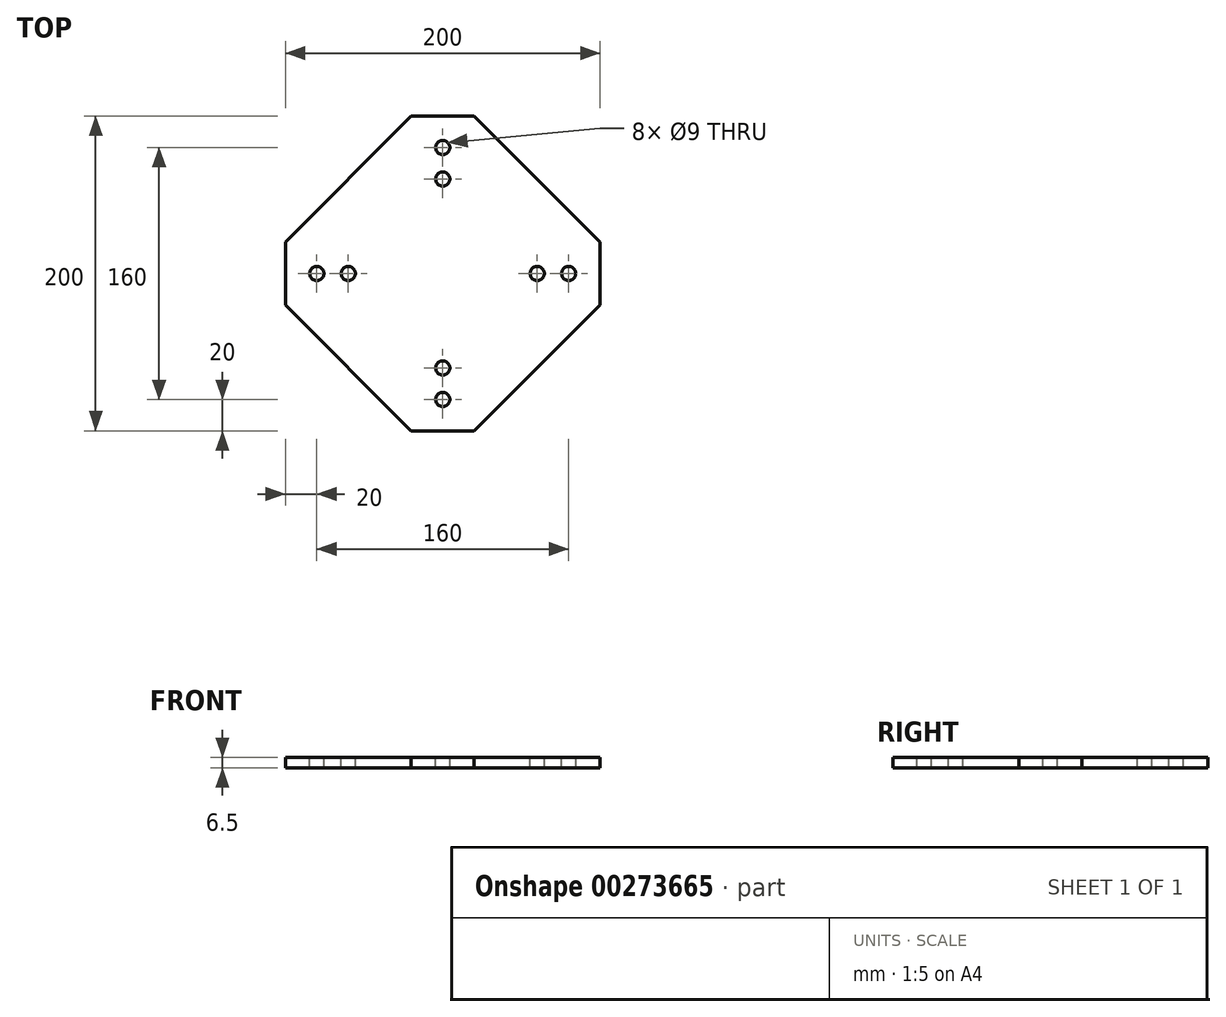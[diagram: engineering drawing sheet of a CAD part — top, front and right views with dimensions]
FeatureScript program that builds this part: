
annotation { "Feature Type Name" : "Feature", "Feature Type Description" : "" }
export const myFeature = defineFeature(function(context is Context, id is Id, definition is map)
    precondition{}
    {
        {
            var Q0;
            Q0=qCreatedBy(makeId("Top.planeOp"),FACE);
            var sketch = newSketch(context, id + "F0", { "sketchPlane" : qUnion([Q0])});
            skLineSegment(sketch, "E0", {"start": v(-100, 20) * mm, "end": v(-20, 100) * mm});
            skLineSegment(sketch, "E1", {"start": v(20, 100) * mm, "end": v(100, 20) * mm});
            skLineSegment(sketch, "E2", {"start": v(100, -20) * mm, "end": v(20, -100) * mm});
            skLineSegment(sketch, "E3", {"start": v(-20, -100) * mm, "end": v(-100, -20) * mm});
            skLineSegment(sketch, "E4", {"start": v(-20, 100) * mm, "end": v(20, 100) * mm});
            skLineSegment(sketch, "E5", {"start": v(-100, -20) * mm, "end": v(-100, 20) * mm});
            skLineSegment(sketch, "E6", {"start": v(100, 20) * mm, "end": v(100, -20) * mm});
            skLineSegment(sketch, "E7", {"start": v(-20, -100) * mm, "end": v(20, -100) * mm});
            skPoint(sketch, "E8.orphan", {"position": v(0, 120) * mm});
            skPoint(sketch, "E9.orphan", {"position": v(120, 0) * mm});
            skPoint(sketch, "E10.orphan", {"position": v(0, -120) * mm});
            skPoint(sketch, "E11.orphan", {"position": v(-120, 0) * mm});
            skSolve(sketch);
        }
        {
            var Q0;
            Q0 = qSketchRegion(id + "F0", true);
            extrude(context, id + "F1", {"entities" : qUnion([Q0]), "depth" : 6.5 * mm});
        }
        {
            var Q0;
            Q0=makeQuery(id+"F1.opExtrude","CAP_FACE",FACE,{"disambiguationData":[OSD([sQuery(id+"F0.wireOp",EDGE,"E0"),sQuery(id+"F0.wireOp",EDGE,"E1"),sQuery(id+"F0.wireOp",EDGE,"E2"),sQuery(id+"F0.wireOp",EDGE,"E3"),sQuery(id+"F0.wireOp",EDGE,"E4"),sQuery(id+"F0.wireOp",EDGE,"E5"),sQuery(id+"F0.wireOp",EDGE,"E6"),sQuery(id+"F0.wireOp",EDGE,"E7")])],"isStart":false});
            var sketch = newSketch(context, id + "F2", { "sketchPlane" : qUnion([Q0])});
            skPoint(sketch, "E12", {"position": v(0, 80) * mm});
            skPoint(sketch, "E13", {"position": v(-80, 0) * mm});
            skLineSegment(sketch, "E14", {"start": v(0, 80) * mm, "end": v(0, -80) * mm, "construction": true});
            skLineSegment(sketch, "E15", {"start": v(-80, 0) * mm, "end": v(80, 0) * mm, "construction": true});
            skPoint(sketch, "E16", {"position": v(0, 60) * mm});
            skPoint(sketch, "E17", {"position": v(0, -60) * mm});
            skPoint(sketch, "E18", {"position": v(-60, 0) * mm});
            skPoint(sketch, "E19", {"position": v(60, 0) * mm});
            skPoint(sketch, "E20", {"position": v(-40, 0) * mm});
            skPoint(sketch, "E21", {"position": v(40, 0) * mm});
            skPoint(sketch, "E22", {"position": v(0, 40) * mm});
            skPoint(sketch, "E23", {"position": v(0, -40) * mm});
            skSolve(sketch);
        }
        {
            var Q0;
            Q0=sQuery(id+"F2.wireOp",VERTEX,"E12");
            var Q1;
            Q1=sQuery(id+"F2.wireOp",VERTEX,"E16");
            var Q2;
            Q2=sQuery(id+"F2.wireOp",VERTEX,"E19");
            var Q3;
            Q3=sQuery(id+"F2.wireOp",VERTEX,"E15.end");
            var Q4;
            Q4=sQuery(id+"F2.wireOp",VERTEX,"E14.end");
            var Q5;
            Q5=sQuery(id+"F2.wireOp",VERTEX,"E17");
            var Q6;
            Q6=sQuery(id+"F2.wireOp",VERTEX,"E13");
            var Q7;
            Q7=sQuery(id+"F2.wireOp",VERTEX,"E18");
            var Q8;
            Q8=makeQuery(id+"F1.opExtrude","SWEPT_BODY",BODY,{"disambiguationData":[OSD([sQuery(id+"F0.wireOp",EDGE,"E0"),sQuery(id+"F0.wireOp",EDGE,"E1"),sQuery(id+"F0.wireOp",EDGE,"E2"),sQuery(id+"F0.wireOp",EDGE,"E3"),sQuery(id+"F0.wireOp",EDGE,"E4"),sQuery(id+"F0.wireOp",EDGE,"E5"),sQuery(id+"F0.wireOp",EDGE,"E6"),sQuery(id+"F0.wireOp",EDGE,"E7")])]});
            hole(context, id + "F3", {"style" : HoleStyle.SIMPLE, "endStyle" : HoleEndStyle.THROUGH, "standardTappedOrClearance" : lookupTablePath({ "fit" : "Normal", "standard" : "ISO", "size" : "M8", "type" : "Clearance" }), "standardBlindInLast" : lookupTablePath({ "fit" : "Normal", "standard" : "ISO", "engagement" : "75%", "pitch" : "1.25 mm", "size" : "M8", "type" : "Clearance & tapped" }), "holeDiameter" : 9 * mm, "majorDiameter" : 5 * mm, "tappedDepth" : 12 * mm, "tapClearance" : 3, "locations" : qUnion([Q0, Q1, Q2, Q3, Q4, Q5, Q6, Q7]), "scope" : qUnion([Q8])});
        }
    });
